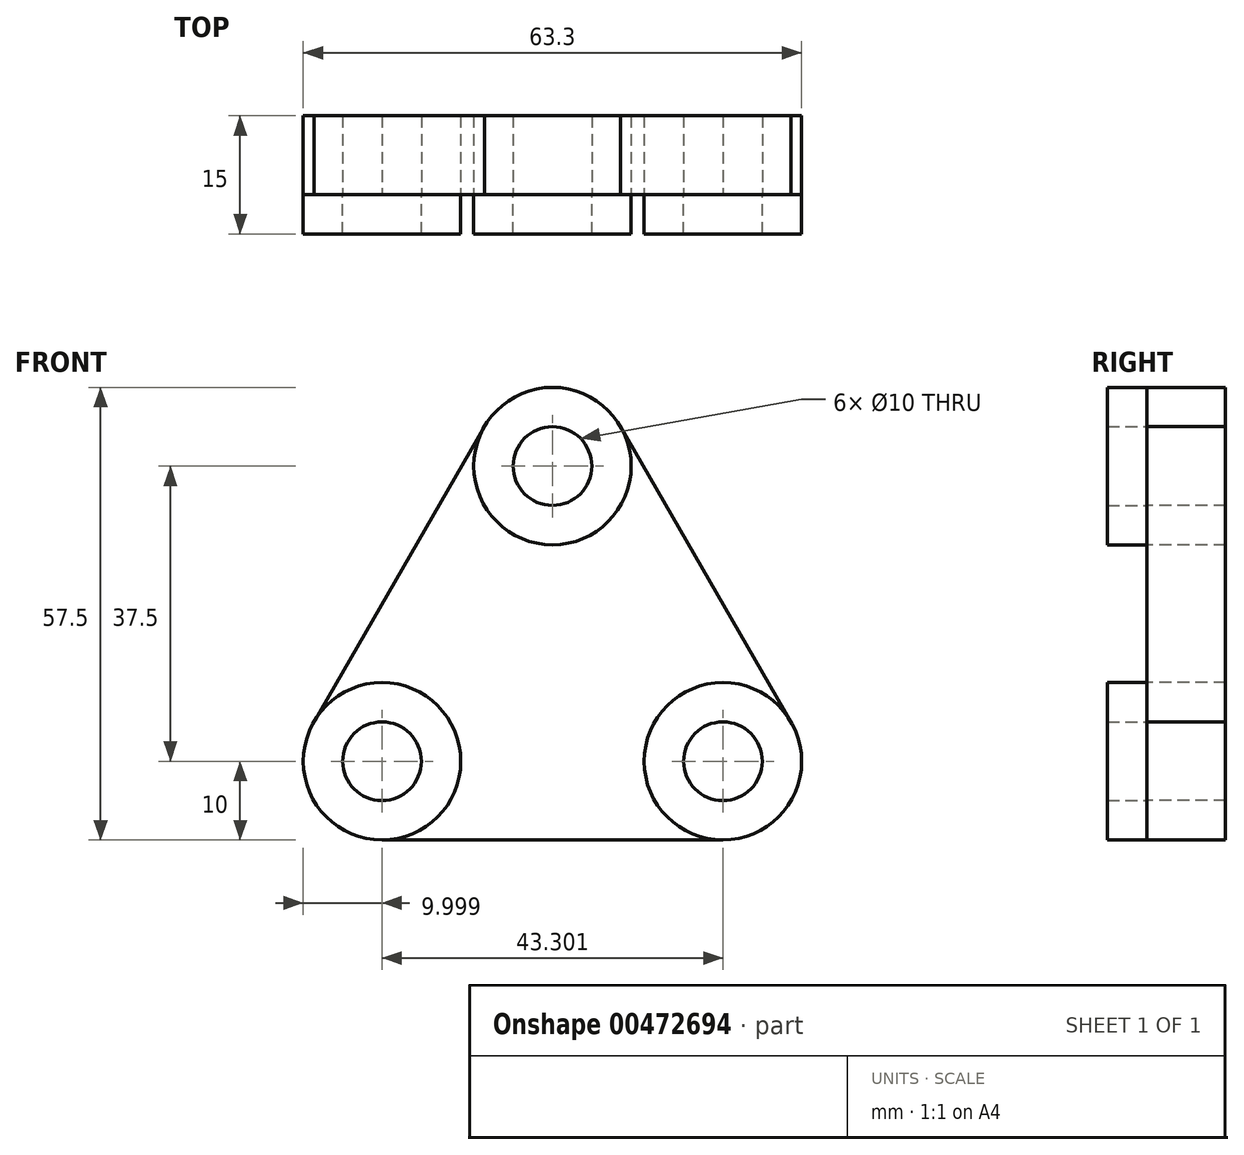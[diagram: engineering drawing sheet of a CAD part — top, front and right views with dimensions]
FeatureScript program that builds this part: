
annotation { "Feature Type Name" : "Feature", "Feature Type Description" : "" }
export const myFeature = defineFeature(function(context is Context, id is Id, definition is map)
    precondition{}
    {
        {
            var Q0;
            Q0=qCreatedBy(makeId("Front.planeOp"),FACE);
            var sketch = newSketch(context, id + "F0", { "sketchPlane" : qUnion([Q0])});
            skCircle(sketch, "E0", {"center": v(0, 25) * mm, "radius": 10 * mm});
            skCircle(sketch, "E1", {"center": v(0, 25) * mm, "radius": 5 * mm});
            skCircle(sketch, "E2", {"center": v(-21.65, -12.5) * mm, "radius": 5 * mm});
            skCircle(sketch, "E3", {"center": v(21.65, -12.5) * mm, "radius": 5 * mm});
            skCircle(sketch, "E4", {"center": v(-21.65, -12.5) * mm, "radius": 10 * mm});
            skCircle(sketch, "E5", {"center": v(21.65, -12.5) * mm, "radius": 10 * mm});
            skLineSegment(sketch, "E6", {"start": v(-30.31, -7.5) * mm, "end": v(-8.66, 30) * mm});
            skLineSegment(sketch, "E7", {"start": v(8.66, 30) * mm, "end": v(30.31, -7.5) * mm});
            skLineSegment(sketch, "E8", {"start": v(-21.65, -22.5) * mm, "end": v(21.65, -22.5) * mm});
            skSolve(sketch);
        }
        {
            var Q0;
            {var subQ0=sQuery(id+"F0.wireOp",EDGE,"E6");Q0=makeQuery(id+"F0.imprint","IMPRINT",FACE,{"disambiguationData":[TD([[makeQuery(id+"F0.imprint","IMPRINT",EDGE,{"derivedFrom":subQ0}),-1.0]])]});}
            extrude(context, id + "F1", {"entities" : qUnion([Q0]), "oppositeDirection" : true, "depth" : 10 * mm});
        }
        {
            var Q0;
            Q0=makeQuery(id+"F0.imprint","IMPRINT",FACE,{"disambiguationData":[TD([[makeQuery(id+"F0.imprint","IMPRINT",EDGE,{"derivedFrom":sQuery(id+"F0.wireOp",EDGE,"E1")}),-1.0]])]});
            var Q1;
            Q1=makeQuery(id+"F0.imprint","IMPRINT",FACE,{"disambiguationData":[TD([[makeQuery(id+"F0.imprint","IMPRINT",EDGE,{"derivedFrom":sQuery(id+"F0.wireOp",EDGE,"E2")}),-1.0]])]});
            var Q2;
            Q2=makeQuery(id+"F0.imprint","IMPRINT",FACE,{"disambiguationData":[TD([[makeQuery(id+"F0.imprint","IMPRINT",EDGE,{"derivedFrom":sQuery(id+"F0.wireOp",EDGE,"E3")}),-1.0]])]});
            extrude(context, id + "F2", {"entities" : qUnion([Q0, Q1, Q2]), "depth" : 5 * mm});
        }
        {
            var Q0;
            Q0=makeQuery(id+"F2.opExtrude","CAP_FACE",FACE,{"disambiguationData":[OSD([sQuery(id+"F0.wireOp",EDGE,"E0"),sQuery(id+"F0.wireOp",EDGE,"E1")])],"isStart":true});
            var Q1;
            Q1=makeQuery(id+"F2.opExtrude","CAP_FACE",FACE,{"disambiguationData":[OSD([sQuery(id+"F0.wireOp",EDGE,"E3"),sQuery(id+"F0.wireOp",EDGE,"E5")])],"isStart":true});
            var Q2;
            Q2=makeQuery(id+"F2.opExtrude","CAP_FACE",FACE,{"disambiguationData":[OSD([sQuery(id+"F0.wireOp",EDGE,"E2"),sQuery(id+"F0.wireOp",EDGE,"E4")])],"isStart":true});
            extrude(context, id + "F3", {"entities" : qUnion([Q0, Q1, Q2]), "depth" : 10 * mm});
        }
    });
